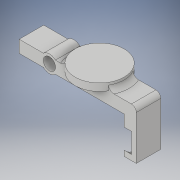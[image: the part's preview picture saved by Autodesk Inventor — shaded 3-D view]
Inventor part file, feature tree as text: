
AUTODESK INVENTOR PART (.ipt)
format: ipt  version: 2019 (Build 230136000, 136)  size: 154,112 bytes
history: native  units: in
note: dims shown in document units (in); Inventor stores cm internally (conversion verified against a paired STEP export)
features: extrude x3, fillet x3, sketch x3
ambient origin geometry x8: Origin, YZ Plane, XZ Plane, XY Plane, X Axis, Y Axis, Z Axis, Center Point
bodies: Solid1 (feature_tree)
feature tree (9):
  extrude  "Extrusion1"  Depth=0.1378in
  extrude  "Extrusion2"  Depth=0.5906in
  fillet  "Fillet1"  Radius=0.1969in
  fillet  "Fillet2"  Radius=0.3937in
  fillet  "Fillet3"  Radius=0.7874in
  extrude  "Extrusion3"  Depth=0.0787in
  sketch  "Sketch1"  dims[d6=0.1969in d7=0.1378in]
  sketch  "Sketch2"  dims[d8=1.1024in d9=0.5906in d10=0.1969in d14=0.3937in d15=0.0in d16=0.7874in]
  sketch  "Sketch3"  dims[d17=0.1181in d18=0.0in d19=0.0787in d20=0.0787in d21=0.0787in d22=0.1181in d23=0.0in]
